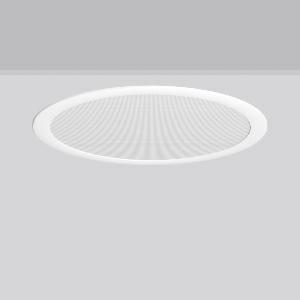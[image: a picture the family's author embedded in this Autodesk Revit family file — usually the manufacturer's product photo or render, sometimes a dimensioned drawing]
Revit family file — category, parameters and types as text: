
# Revit family: toledo_flat_round_e_901586_002_e46f
name_source: partatom
category: Lighting Fixtures
units: mm (PartAtom-declared; Revit-internal decimal feet)

## family parameters
Cut with Voids When Loaded = No
Host = Face
Light Source = No
Part Type = Normal
Room Calculation Point = No
Round Connector Dimension = Use Diameter
Shared = No

## types (1)
- TOLEDO FLAT round E (1 x LED Modul 830, 3450 lm, 3000)
    Apparent Load = 30 VA
    CIE Flux Codes = 62 86 96 100 100
    Color Rendering = 80
    Color Temperature = 3000
    Default Elevation = 1800 mm
    Description = Series: TOLEDO FLAT round
Ultra thin recessed downlight. Housing: die-cast aluminium. Lightguide and diffuser made of non-yellowing PMMA, prismatic. Ceiling installation with spring system. Mounting depth depends on ceiling strength. Including separate LED converter with connecting cable 250 mm. Suitable for through-wiring with separately available accessories. Surface mounted housing as accessory for all sizes. Retrofittable decorative cylinders made of chintz fabric as accessory, optional with satin finish plastic diffuser. Through-wiring box (5 pole) available as accessory. 
Colour: white
Diameter: 495 mm
Height: 6 mm
Cut-out diameter: 470 mm
Recess height: 40-59 mm
Luminaire: recess height: 31-51 mm
Lamp: LED
Socket: without socket
Colour temperature: 3000K
Colour rendering index (CRI): 80
System power: 30 W
Rated luminous flux: 3450 lm
Luminous efficiency: 115 lm/W
Control gear: Regulated power supply
Protection class: II
Type of protection: IP 54
    Height = 0 mm  [stored 0 ft]
    Lamp = 1 x LED Modul 830
    Lamp Light Flux = 3450 lm
    Lamp count = 1
    Length = 495 mm
    Lifetime = 50000 h
    Luminous efficacy = 115 lm/W
    Manufacturer = RZB
    ModVariant = No
    Model = 901586.002
    Mounting Place = Ceiling
    Mounting Type = Recessed
    Number of Poles = 1
    OnlyDefault = Yes
    Power Factor = 1
    Product Name = TOLEDO FLAT round E
    Product group = Recessed downlights
    ProductGroupID = 402
    Protection Class = Protection class II
    Protection Degree = IP 20
    RLX_Detail_Level = 1
    RLX_Emergency_Light_Flux = 0 lm
    RLX_Emergency_Type = 0
    RLX_Emergency_Type_DB = No
    RlxData = <blob elided: 38245 chars, md5=3bad5b70>
    Socket = socket
    Standby Power = 0 W
    System Light Flux = 3450 lm
    System Power = 30 W
    Type Comments = Product without accessories
    Type Image = 901586.002.jpg
    URL = http://relux.com
    VarID = ---
    Voltage = 230 V
    Voltage Range = 220-240 V
    Weight = 0.00 kg
    Width = 0 mm  [stored 0 ft]

note: [stored X ft] marks values corroborated as IEEE doubles in the binary element streams (Revit-internal decimal feet)

## geometry (parser evidence)
native form markers: Blend x4, Sweep x9
no freeform markers — native parametric forms only
